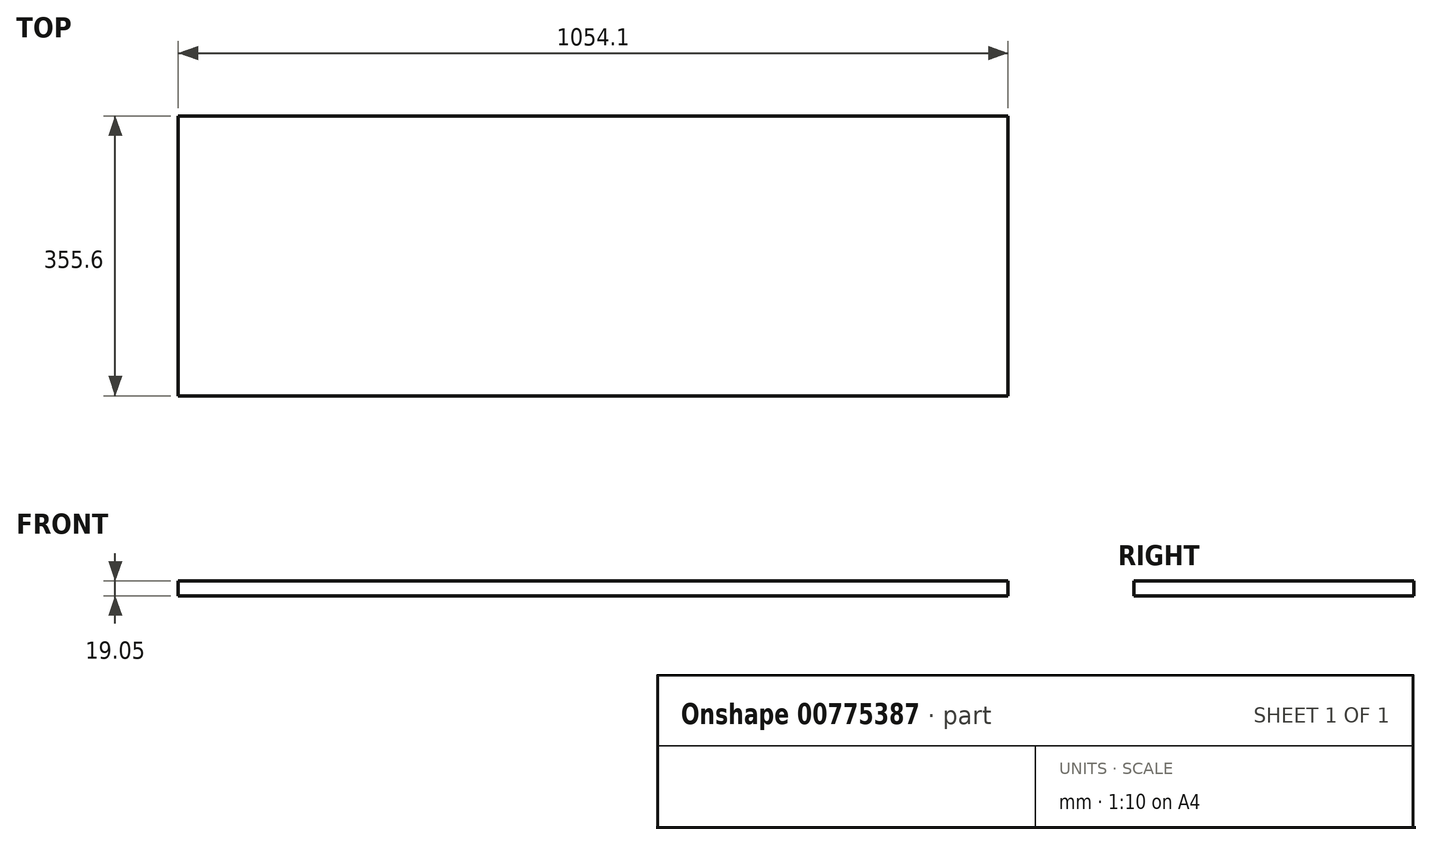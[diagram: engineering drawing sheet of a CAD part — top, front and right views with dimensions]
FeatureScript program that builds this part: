
annotation { "Feature Type Name" : "Feature", "Feature Type Description" : "" }
export const myFeature = defineFeature(function(context is Context, id is Id, definition is map)
    precondition{}
    {
        {
            var Q0;
            Q0=qCreatedBy(makeId("Top.planeOp"),FACE);
            var sketch = newSketch(context, id + "F0", { "sketchPlane" : qUnion([Q0])});
            skLineSegment(sketch, "E0.bottom", {"start": v(527.05, 177.8) * mm, "end": v(-527.05, 177.8) * mm});
            skLineSegment(sketch, "E0.top", {"start": v(527.05, -177.8) * mm, "end": v(-527.05, -177.8) * mm});
            skLineSegment(sketch, "E0.left", {"start": v(527.05, 177.8) * mm, "end": v(527.05, -177.8) * mm});
            skLineSegment(sketch, "E0.right", {"start": v(-527.05, 177.8) * mm, "end": v(-527.05, -177.8) * mm});
            skPoint(sketch, "E0.middle", {"position": v(0, 0) * mm});
            skSolve(sketch);
        }
        {
            var Q0;
            Q0=makeQuery(id+"F0.imprint","IMPRINT",FACE,{"disambiguationData":[TD([[makeQuery(id+"F0.imprint","IMPRINT",EDGE,{"derivedFrom":sQuery(id+"F0.wireOp",EDGE,"E0.bottom")}),1.0]])]});
            extrude(context, id + "F1", {"entities" : qUnion([Q0]), "depth" : 19.05 * mm, "offsetDistance" : 25.4 * mm});
        }
    });
